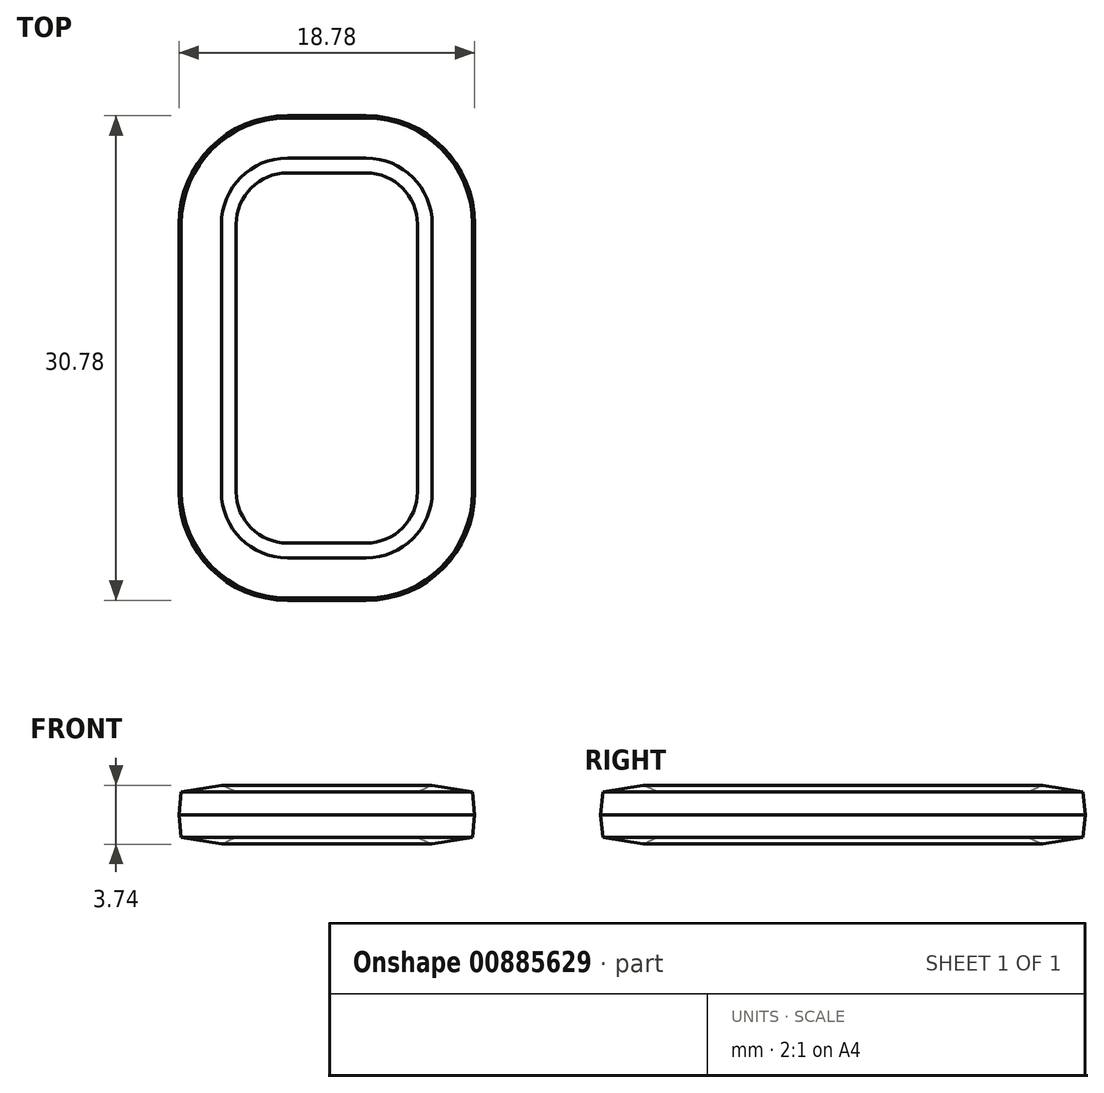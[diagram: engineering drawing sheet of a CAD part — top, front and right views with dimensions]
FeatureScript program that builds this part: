
annotation { "Feature Type Name" : "Feature", "Feature Type Description" : "" }
export const myFeature = defineFeature(function(context is Context, id is Id, definition is map)
    precondition{}
    {
        {
            var Q0;
            Q0=qCreatedBy(makeId("Top.planeOp"),FACE);
            var sketch = newSketch(context, id + "F0", { "sketchPlane" : qUnion([Q0])});
            skLineSegment(sketch, "E0.bottom", {"start": v(2.5, -13.5) * mm, "end": v(-2.5, -13.5) * mm});
            skLineSegment(sketch, "E0.top", {"start": v(2.5, 13.5) * mm, "end": v(-2.5, 13.5) * mm});
            skLineSegment(sketch, "E0.left", {"start": v(7.5, -8.5) * mm, "end": v(7.5, 8.5) * mm});
            skLineSegment(sketch, "E0.right", {"start": v(-7.5, -8.5) * mm, "end": v(-7.5, 8.5) * mm});
            skPoint(sketch, "E0.middle", {"position": v(0, 0) * mm});
            skPoint(sketch, "E1.visualSharp", {"position": v(-7.5, 13.5) * mm});
            skArc(sketch, "E1.filletArc", {"start": v(-2.5, 13.5) * mm, "mid": v(-6.04, 12.04) * mm, "end": v(-7.5, 8.5) * mm});
            skPoint(sketch, "E2.visualSharp", {"position": v(-7.5, -13.5) * mm});
            skArc(sketch, "E2.filletArc", {"start": v(-7.5, -8.5) * mm, "mid": v(-6.04, -12.04) * mm, "end": v(-2.5, -13.5) * mm});
            skPoint(sketch, "E3.visualSharp", {"position": v(7.5, -13.5) * mm});
            skArc(sketch, "E3.filletArc", {"start": v(2.5, -13.5) * mm, "mid": v(6.04, -12.04) * mm, "end": v(7.5, -8.5) * mm});
            skPoint(sketch, "E4.visualSharp", {"position": v(7.5, 13.5) * mm});
            skArc(sketch, "E4.filletArc", {"start": v(7.5, 8.5) * mm, "mid": v(6.04, 12.04) * mm, "end": v(2.5, 13.5) * mm});
            skSolve(sketch);
        }
        {
            var Q0;
            Q0=qCreatedBy(makeId("Front.planeOp"),FACE);
            var sketch = newSketch(context, id + "F1", { "sketchPlane" : qUnion([Q0])});
            skPoint(sketch, "E5.middle", {"position": v(-7.49, 0) * mm});
            skLineSegment(sketch, "E6", {"start": v(-6.7, 1.87) * mm, "end": v(-9.25, 1.45) * mm});
            skLineSegment(sketch, "E7", {"start": v(-5.75, 1.45) * mm, "end": v(-6.7, 1.87) * mm});
            skLineSegment(sketch, "E8", {"start": v(-9.25, 1.45) * mm, "end": v(-9.4, 0) * mm});
            skLineSegment(sketch, "E9", {"start": v(-5.75, 1.45) * mm, "end": v(-5.75, 0) * mm});
            skLineSegment(sketch, "E10.MirrorCS", {"start": v(-5.75, -1.45) * mm, "end": v(-5.75, 0) * mm});
            skLineSegment(sketch, "E11.MirrorCS", {"start": v(-5.75, -1.45) * mm, "end": v(-6.7, -1.87) * mm});
            skLineSegment(sketch, "E12.MirrorCS", {"start": v(-9.25, -1.45) * mm, "end": v(-9.4, 0) * mm});
            skLineSegment(sketch, "E13.MirrorCS", {"start": v(-6.7, -1.87) * mm, "end": v(-9.25, -1.45) * mm});
            skSolve(sketch);
        }
        {
            var Q0;
            Q0=makeQuery(id+"F1.imprint","IMPRINT",FACE,{"disambiguationData":[TD([[makeQuery(id+"F1.imprint","IMPRINT",EDGE,{"derivedFrom":sQuery(id+"F1.wireOp",EDGE,"E5.bottom")}),-1.0]])]});
            var Q1;
            Q1=makeQuery(id+"F1.imprint","IMPRINT",FACE,{"disambiguationData":[TD([[makeQuery(id+"F1.imprint","IMPRINT",EDGE,{"derivedFrom":sQuery(id+"F1.wireOp",EDGE,"E6")}),1.0]])]});
            var Q2;
            Q2=sQuery(id+"F0.wireOp",EDGE,"E0.right");
            var Q3;
            Q3=sQuery(id+"F0.wireOp",EDGE,"E1.filletArc");
            var Q4;
            Q4=sQuery(id+"F0.wireOp",EDGE,"E0.top");
            var Q5;
            Q5=sQuery(id+"F0.wireOp",EDGE,"E4.filletArc");
            var Q6;
            Q6=sQuery(id+"F0.wireOp",EDGE,"E0.left");
            var Q7;
            Q7=sQuery(id+"F0.wireOp",EDGE,"E3.filletArc");
            var Q8;
            Q8=sQuery(id+"F0.wireOp",EDGE,"E0.bottom");
            var Q9;
            Q9=sQuery(id+"F0.wireOp",EDGE,"E2.filletArc");
            sweep(context, id + "F2", {"profiles" : qUnion([Q0, Q1]), "path" : qUnion([Q2, Q3, Q4, Q5, Q6, Q7, Q8, Q9])});
        }
    });
